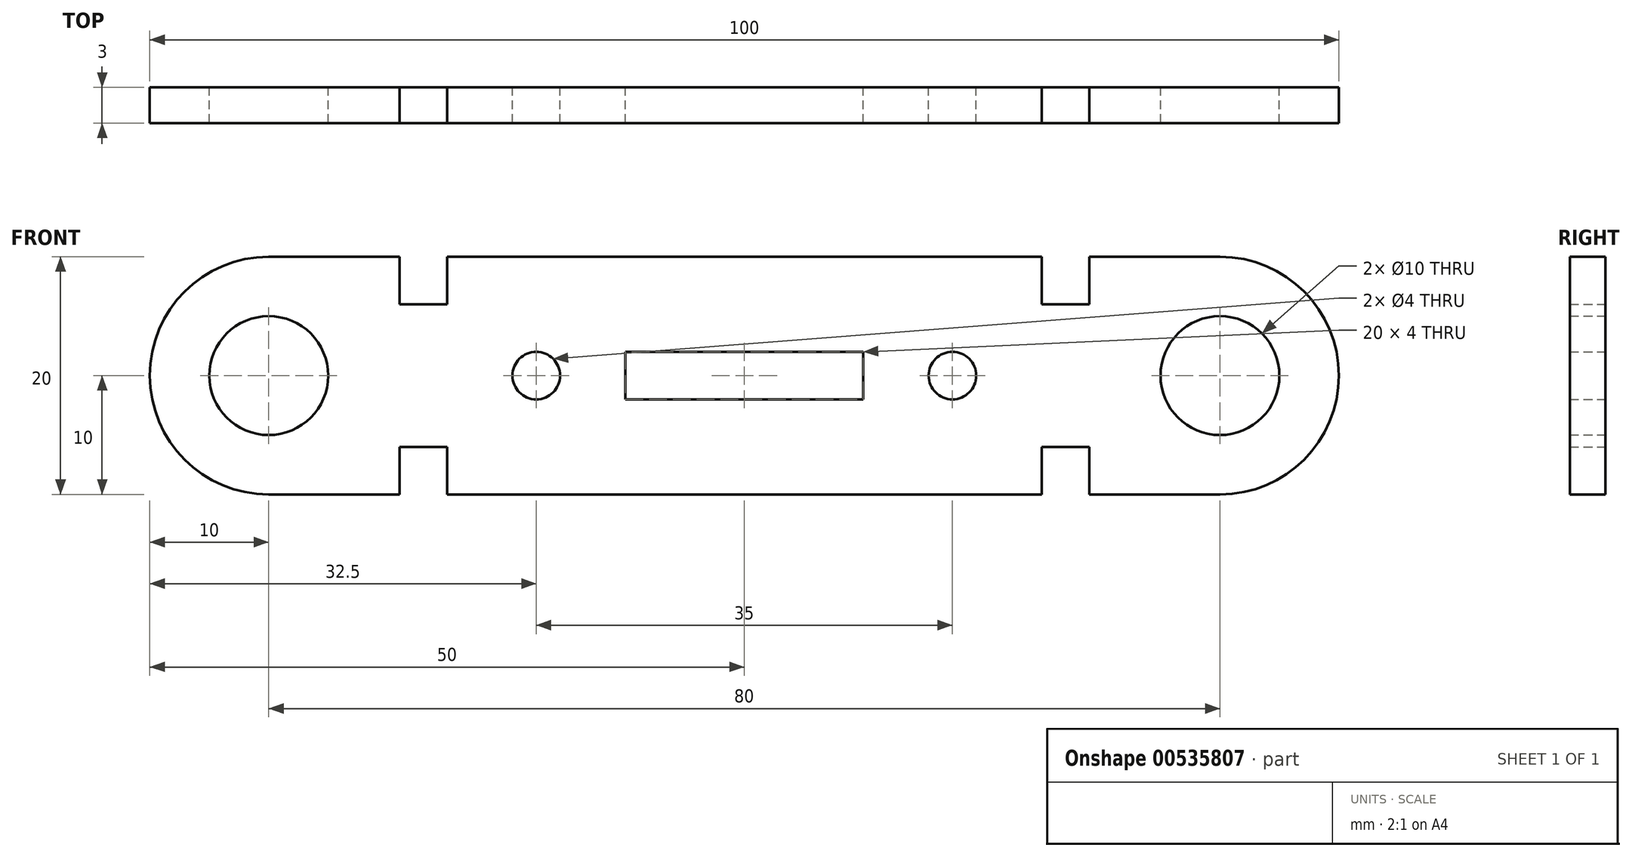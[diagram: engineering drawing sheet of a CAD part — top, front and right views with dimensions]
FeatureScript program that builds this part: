
annotation { "Feature Type Name" : "Feature", "Feature Type Description" : "" }
export const myFeature = defineFeature(function(context is Context, id is Id, definition is map)
    precondition{}
    {
        {
            var Q0;
            Q0=qCreatedBy(makeId("Front.planeOp"),FACE);
            var sketch = newSketch(context, id + "F0", { "sketchPlane" : qUnion([Q0])});
            skCircle(sketch, "E0", {"center": v(-40, 0) * mm, "radius": 5 * mm});
            skCircle(sketch, "E1.MirrorC", {"center": v(40, 0) * mm, "radius": 5 * mm});
            skArc(sketch, "E2", {"start": v(-40, 10) * mm, "mid": v(-50, 0) * mm, "end": v(-40, -10) * mm});
            skArc(sketch, "E3.MirrorC", {"start": v(40, 10) * mm, "mid": v(50, 0) * mm, "end": v(40, -10) * mm});
            skLineSegment(sketch, "E4", {"start": v(-40, 10) * mm, "end": v(-29, 10) * mm});
            skLineSegment(sketch, "E5.MirrorCS", {"start": v(-40, -10) * mm, "end": v(-29, -10) * mm});
            skCircle(sketch, "E6", {"center": v(-17.5, 0) * mm, "radius": 2 * mm});
            skCircle(sketch, "E7.MirrorC", {"center": v(17.5, 0) * mm, "radius": 2 * mm});
            skLineSegment(sketch, "E8.bottom", {"start": v(-10, 2) * mm, "end": v(10, 2) * mm});
            skLineSegment(sketch, "E8.top", {"start": v(-10, -2) * mm, "end": v(10, -2) * mm});
            skLineSegment(sketch, "E8.left", {"start": v(-10, 2) * mm, "end": v(-10, -2) * mm});
            skLineSegment(sketch, "E8.right", {"start": v(10, 2) * mm, "end": v(10, -2) * mm});
            skPoint(sketch, "E8.middle", {"position": v(0, 0) * mm});
            skLineSegment(sketch, "E9.top", {"start": v(-29, 6) * mm, "end": v(-25, 6) * mm});
            skLineSegment(sketch, "E9.left", {"start": v(-29, 10) * mm, "end": v(-29, 6) * mm});
            skLineSegment(sketch, "E9.right", {"start": v(-25, 10) * mm, "end": v(-25, 6) * mm});
            skLineSegment(sketch, "E10.trimOffspring", {"start": v(-25, 10) * mm, "end": v(25, 10) * mm});
            skLineSegment(sketch, "E11.MirrorCS", {"start": v(29, 10) * mm, "end": v(29, 6) * mm});
            skLineSegment(sketch, "E12.MirrorCS", {"start": v(29, 6) * mm, "end": v(25, 6) * mm});
            skLineSegment(sketch, "E13.MirrorCS", {"start": v(25, 10) * mm, "end": v(25, 6) * mm});
            skLineSegment(sketch, "E14.MirrorCS", {"start": v(-29, -6) * mm, "end": v(-25, -6) * mm});
            skLineSegment(sketch, "E15.MirrorCS", {"start": v(-29, -10) * mm, "end": v(-29, -6) * mm});
            skLineSegment(sketch, "E16.MirrorCS", {"start": v(-25, -10) * mm, "end": v(-25, -6) * mm});
            skLineSegment(sketch, "E17.MirrorCS", {"start": v(29, -10) * mm, "end": v(29, -6) * mm});
            skLineSegment(sketch, "E18.MirrorCS", {"start": v(25, -10) * mm, "end": v(25, -6) * mm});
            skLineSegment(sketch, "E19.MirrorCS", {"start": v(29, -6) * mm, "end": v(25, -6) * mm});
            skLineSegment(sketch, "E20.trimOffspring", {"start": v(-25, -10) * mm, "end": v(25, -10) * mm});
            skLineSegment(sketch, "E21.trimOffspring", {"start": v(29, -10) * mm, "end": v(40, -10) * mm});
            skLineSegment(sketch, "E22.trimOffspring", {"start": v(29, 10) * mm, "end": v(40, 10) * mm});
            skSolve(sketch);
        }
        {
            var Q0;
            Q0 = qSketchRegion(id + "F0", true);
            extrude(context, id + "F1", {"entities" : qUnion([Q0]), "depth" : 3 * mm, "offsetDistance" : 25 * mm});
        }
    });
